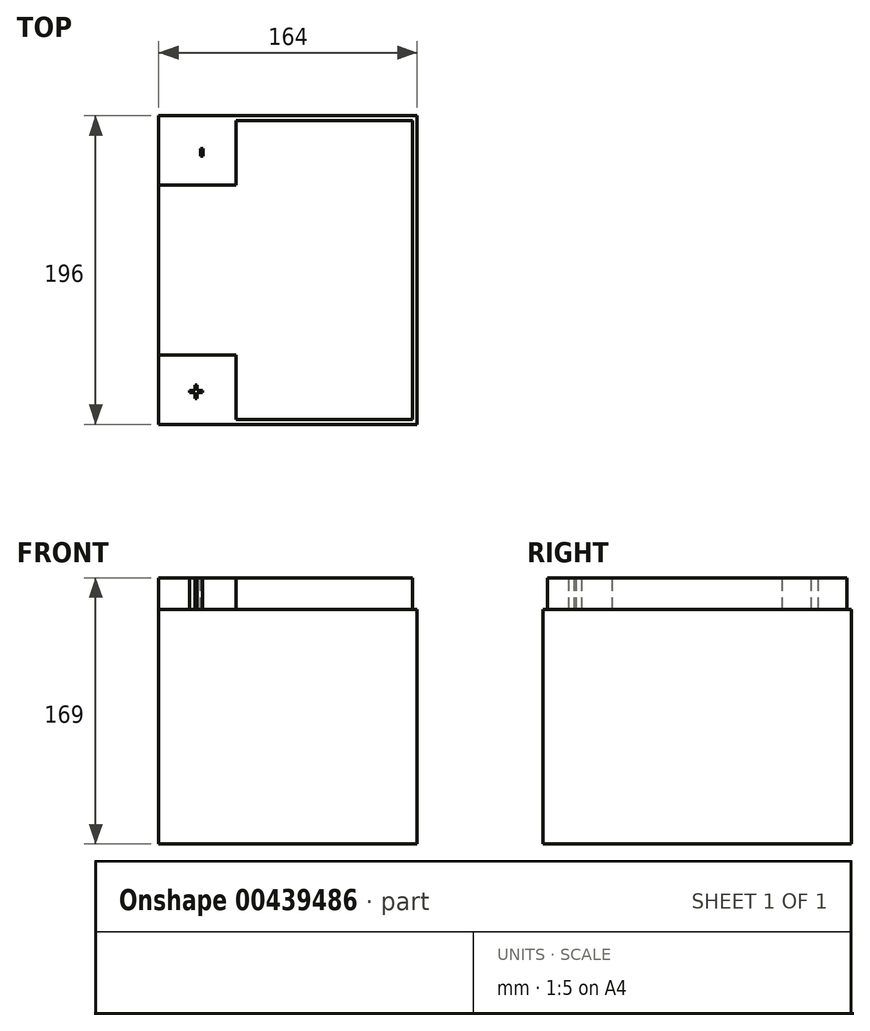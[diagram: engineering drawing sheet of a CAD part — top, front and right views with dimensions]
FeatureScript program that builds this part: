
annotation { "Feature Type Name" : "Feature", "Feature Type Description" : "" }
export const myFeature = defineFeature(function(context is Context, id is Id, definition is map)
    precondition{}
    {
        {
            var Q0;
            Q0=qCreatedBy(makeId("Front.planeOp"),FACE);
            var sketch = newSketch(context, id + "F0", { "sketchPlane" : qUnion([Q0])});
            skLineSegment(sketch, "E0.bottom", {"start": v(-164, 169) * mm, "end": v(0, 169) * mm});
            skLineSegment(sketch, "E0.top", {"start": v(-164, 0) * mm, "end": v(0, 0) * mm});
            skLineSegment(sketch, "E0.left", {"start": v(-164, 169) * mm, "end": v(-164, 0) * mm});
            skLineSegment(sketch, "E0.right", {"start": v(0, 169) * mm, "end": v(0, 0) * mm});
            skSolve(sketch);
        }
        {
            var Q0;
            Q0=makeQuery(id+"F0.imprint","IMPRINT",FACE,{"disambiguationData":[TD([[makeQuery(id+"F0.imprint","IMPRINT",EDGE,{"derivedFrom":sQuery(id+"F0.wireOp",EDGE,"E0.bottom")}),-1.0]])]});
            extrude(context, id + "F1", {"entities" : qUnion([Q0]), "offsetDistance" : 25 * mm, "depth" : 196 * mm});
        }
        {
            var Q0;
            Q0=makeQuery(id+"F1.opExtrude","SWEPT_FACE",FACE,{"disambiguationData":[OSD([sQuery(id+"F0.wireOp",EDGE,"E0.bottom")])]});
            var sketch = newSketch(context, id + "F2", { "sketchPlane" : qUnion([Q0])});
            skLineSegment(sketch, "E1.bottom", {"start": v(-164, 0) * mm, "end": v(-115, 0) * mm});
            skLineSegment(sketch, "E1.top", {"start": v(-164, -44) * mm, "end": v(-115, -44) * mm});
            skLineSegment(sketch, "E1.left", {"start": v(-164, 0) * mm, "end": v(-164, -44) * mm});
            skLineSegment(sketch, "E1.right", {"start": v(-115, 0) * mm, "end": v(-115, -44) * mm});
            skLineSegment(sketch, "E2.bottom", {"start": v(-164, -196) * mm, "end": v(-115, -196) * mm});
            skLineSegment(sketch, "E2.top", {"start": v(-164, -152) * mm, "end": v(-115, -152) * mm});
            skLineSegment(sketch, "E2.left", {"start": v(-164, -196) * mm, "end": v(-164, -152) * mm});
            skLineSegment(sketch, "E2.right", {"start": v(-115, -196) * mm, "end": v(-115, -152) * mm});
            skText(sketch, "E3", { "text": "+", "fontName": "OpenSans-Regular.ttf"});
            skText(sketch, "E4", { "text": "-", "fontName": "OpenSans-Regular.ttf"});
            skLineSegment(sketch, "E5", {"start": v(-115, -193) * mm, "end": v(-3, -193) * mm});
            skLineSegment(sketch, "E6", {"start": v(-3, -193) * mm, "end": v(-3, -3) * mm});
            skLineSegment(sketch, "E7", {"start": v(-3, -3) * mm, "end": v(-115, -3) * mm});
            const initialGuessF2  = {"E3": [-0.14535, -0.18142, 1, 0, 0.01249], "E4": [-0.1317, -0.0263, 0, 1, 0.01347]};
            skSetInitialGuess(sketch, initialGuessF2);
            skSolve(sketch);
        }
        {
            var Q0;
            Q0=makeQuery(id+"F2.imprint","IMPRINT",FACE,{"disambiguationData":[TD([[makeQuery(id+"F2.imprint","IMPRINT",EDGE,{"derivedFrom":sQuery(id+"F2.wireOp",EDGE,"E1.bottom")}),-1.0]])]});
            var Q1;
            Q1=makeQuery(id+"F2.imprint","IMPRINT",FACE,{"disambiguationData":[TD([[makeQuery(id+"F2.imprint","IMPRINT",EDGE,{"derivedFrom":sQuery(id+"F2.wireOp",EDGE,"E2.bottom")}),1.0]])]});
            var Q2;
            {var subQ0=sQuery(id+"F2.wireOp",EDGE,"E5");Q2=makeQuery(id+"F2.imprint","IMPRINT",FACE,{"disambiguationData":[TD([[makeQuery(id+"F2.imprint","IMPRINT",EDGE,{"derivedFrom":subQ0}),-1.0]])]});}
            extrude(context, id + "F3", {"entities" : qUnion([Q0, Q1, Q2]), "operationType" : NewBodyOperationType.REMOVE, "oppositeDirection" : true, "offsetDistance" : 25 * mm, "depth" : 20 * mm});
        }
    });
